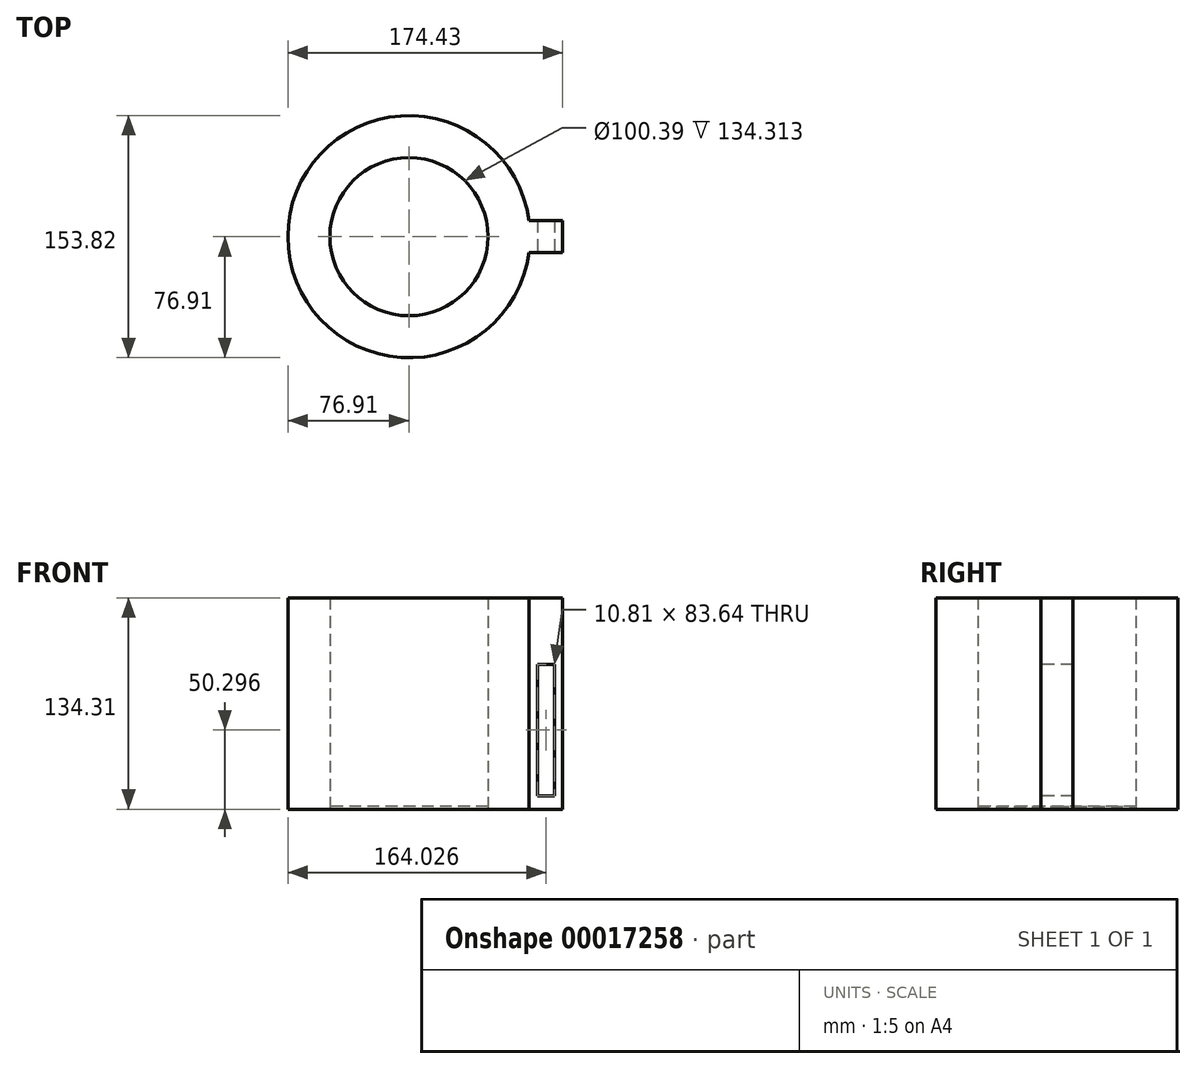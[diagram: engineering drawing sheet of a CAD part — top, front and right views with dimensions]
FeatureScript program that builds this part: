
annotation { "Feature Type Name" : "Feature", "Feature Type Description" : "" }
export const myFeature = defineFeature(function(context is Context, id is Id, definition is map)
    precondition{}
    {
        {
            var Q0;
            Q0=qCreatedBy(makeId("Top.planeOp"),FACE);
            var sketch = newSketch(context, id + "F0", { "sketchPlane" : qUnion([Q0])});
            skCircle(sketch, "E0", {"center": v(0, 0) * mm, "radius": 76.9 * mm});
            skCircle(sketch, "E1", {"center": v(0, 0) * mm, "radius": 50.2 * mm});
            skLineSegment(sketch, "E2.rect.bottom", {"start": v(56.3, 10.09) * mm, "end": v(97.52, 10.09) * mm});
            skLineSegment(sketch, "E2.rect.top", {"start": v(56.3, -10.09) * mm, "end": v(97.52, -10.09) * mm});
            skLineSegment(sketch, "E2.rect.left", {"start": v(56.3, 10.09) * mm, "end": v(56.3, -10.09) * mm});
            skLineSegment(sketch, "E2.rect.right", {"start": v(97.52, 10.09) * mm, "end": v(97.52, -10.09) * mm});
            skPoint(sketch, "E2.rect.middle", {"position": v(76.9, 0) * mm});
            skSolve(sketch);
        }
        {
            var Q0;
            {var subQ0=sQuery(id+"F0.wireOp",EDGE,"E2.rect.left");Q0=makeQuery(id+"F0.imprint","IMPRINT",FACE,{"disambiguationData":[TD([[makeQuery(id+"F0.imprint","IMPRINT",EDGE,{"derivedFrom":subQ0}),1.0]])]});}
            var Q1;
            {var subQ0=sQuery(id+"F0.wireOp",EDGE,"E2.rect.right");Q1=makeQuery(id+"F0.imprint","IMPRINT",FACE,{"disambiguationData":[TD([[makeQuery(id+"F0.imprint","IMPRINT",EDGE,{"derivedFrom":subQ0}),-1.0]])]});}
            var Q2;
            Q2=makeQuery(id+"F0.imprint","IMPRINT",FACE,{"disambiguationData":[TD([[makeQuery(id+"F0.imprint","IMPRINT",EDGE,{"derivedFrom":sQuery(id+"F0.wireOp",EDGE,"E1")}),-1.0]])]});
            extrude(context, id + "F1", {"entities" : qUnion([Q0, Q1, Q2]), "depth" : 134.3 * mm});
        }
        {
            var Q0;
            Q0=makeQuery(id+"F1.opExtrude","SWEPT_FACE",FACE,{"disambiguationData":[OSD([sQuery(id+"F0.wireOp",EDGE,"E2.rect.top")])]});
            var sketch = newSketch(context, id + "F2", { "sketchPlane" : qUnion([Q0])});
            skLineSegment(sketch, "E3.rect.bottom", {"start": v(92.52, 92.12) * mm, "end": v(81.71, 92.12) * mm});
            skLineSegment(sketch, "E3.rect.top", {"start": v(92.52, 8.47) * mm, "end": v(81.71, 8.47) * mm});
            skLineSegment(sketch, "E3.rect.left", {"start": v(92.52, 92.12) * mm, "end": v(92.52, 8.47) * mm});
            skLineSegment(sketch, "E3.rect.right", {"start": v(81.71, 92.12) * mm, "end": v(81.71, 8.47) * mm});
            skPoint(sketch, "E3.rect.middle", {"position": v(87.12, 50.3) * mm});
            skSolve(sketch);
        }
        {
            var Q0;
            Q0=makeQuery(id+"F2.imprint","IMPRINT",FACE,{"disambiguationData":[TD([[makeQuery(id+"F2.imprint","IMPRINT",EDGE,{"derivedFrom":sQuery(id+"F2.wireOp",EDGE,"E3.rect.bottom")}),1.0]])]});
            extrude(context, id + "F3", {"entities" : qUnion([Q0]), "operationType" : NewBodyOperationType.REMOVE, "oppositeDirection" : true, "depth" : 25.4 * mm});
        }
        {
            var Q0;
            Q0=makeQuery(id+"F1.opExtrude","CAP_FACE",FACE,{"disambiguationData":[OSD([sQuery(id+"F0.wireOp",EDGE,"E0"),sQuery(id+"F0.wireOp",EDGE,"E1"),sQuery(id+"F0.wireOp",EDGE,"E2.rect.bottom"),sQuery(id+"F0.wireOp",EDGE,"E2.rect.top"),sQuery(id+"F0.wireOp",EDGE,"E2.rect.right")])],"isStart":true});
            var sketch = newSketch(context, id + "F4", { "sketchPlane" : qUnion([Q0])});
            skCircle(sketch, "E4", {"center": v(0, 0) * mm, "radius": 50.88 * mm});
            skSolve(sketch);
        }
        {
            var Q0;
            Q0=makeQuery(id+"F4.imprint","IMPRINT",FACE,{"disambiguationData":[TD([[makeQuery(id+"F4.imprint","IMPRINT",EDGE,{"derivedFrom":makeQuery(id+"F1.opExtrude","CAP_EDGE",EDGE,{"disambiguationData":[OSD([sQuery(id+"F0.wireOp",EDGE,"E1")])],"isStart":true})}),-1.0]])]});
            extrude(context, id + "F5", {"entities" : qUnion([Q0]), "oppositeDirection" : true, "depth" : 1.92 * mm});
        }
    });
